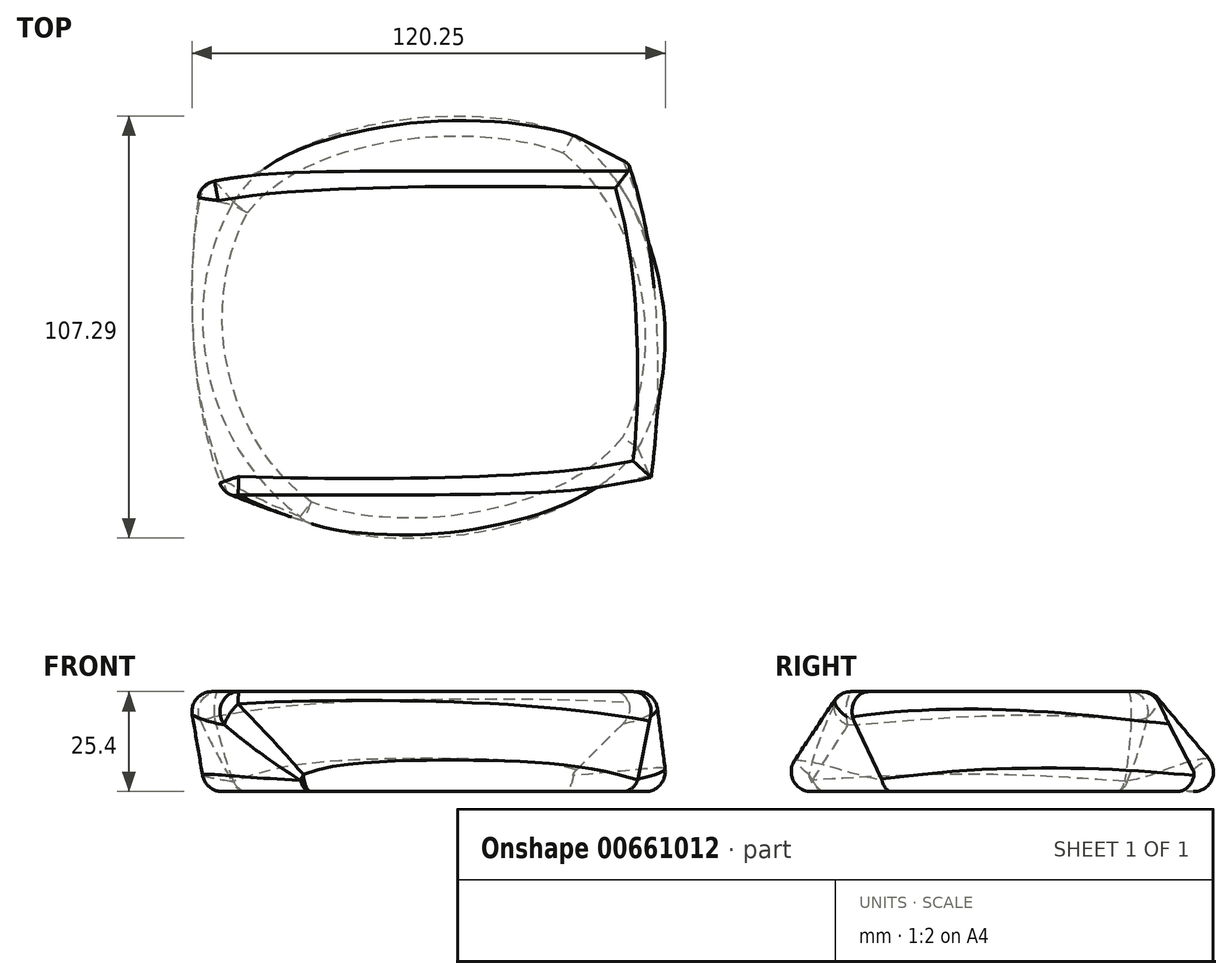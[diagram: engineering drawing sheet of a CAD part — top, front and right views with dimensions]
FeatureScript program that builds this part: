
annotation { "Feature Type Name" : "Feature", "Feature Type Description" : "" }
export const myFeature = defineFeature(function(context is Context, id is Id, definition is map)
    precondition{}
    {
        {
            var Q0;
            Q0=qCreatedBy(makeId("Top.planeOp"),FACE);
            var sketch = newSketch(context, id + "F0", { "sketchPlane" : qUnion([Q0])});
            skCircle(sketch, "E0", {"center": v(0, 0) * mm, "radius": 58.75 * mm});
            skSolve(sketch);
        }
        {
            var Q0;
            Q0=qCreatedBy(makeId("Top.planeOp"),FACE);
            cPlane(context, id + "F1", {"entities" : qUnion([Q0]), "cplaneType" : CPlaneType.OFFSET, "offset" : 25.4 * mm, "width" : 152.4 * mm, "height" : 152.4 * mm});
        }
        {
            var Q0;
            Q0=qCreatedBy(id+"F1.planeOp",FACE);
            var sketch = newSketch(context, id + "F2", { "sketchPlane" : qUnion([Q0])});
            skLineSegment(sketch, "E1.bottom", {"start": v(-63.13, 37.36) * mm, "end": v(55.54, 37.36) * mm});
            skLineSegment(sketch, "E1.top", {"start": v(-63.13, -41.93) * mm, "end": v(55.54, -41.93) * mm});
            skLineSegment(sketch, "E1.left", {"start": v(-63.13, 37.36) * mm, "end": v(-63.13, -41.93) * mm});
            skLineSegment(sketch, "E1.right", {"start": v(55.54, 37.36) * mm, "end": v(55.54, -41.93) * mm});
            skSolve(sketch);
        }
        {
            var Q0;
            Q0=makeQuery(id+"F2.imprint","IMPRINT",FACE,{"disambiguationData":[TD([[makeQuery(id+"F2.imprint","IMPRINT",EDGE,{"derivedFrom":sQuery(id+"F2.wireOp",EDGE,"E1.bottom")}),-1.0]])]});
            var Q1;
            Q1=makeQuery(id+"F0.imprint","IMPRINT",FACE,{"disambiguationData":[TD([[makeQuery(id+"F0.imprint","IMPRINT",EDGE,{"derivedFrom":sQuery(id+"F0.wireOp",EDGE,"E0")}),1.0]])]});
            loft(context, id + "F3", {"sheetProfilesArray" : [{ "sheetProfileEntities" : qUnion([Q0]) }, { "sheetProfileEntities" : qUnion([Q1]) }]});
        }
        {
            var Q0;
            Q0=makeQuery(id+"F3.opLoft","MID_CAP_EDGE",EDGE,{"disambiguationData":[OSD([sQuery(id+"F2.wireOp",EDGE,"E1.bottom"),sQuery(id+"F2.wireOp",EDGE,"E1.top"),sQuery(id+"F2.wireOp",EDGE,"E1.left")])],"capPos":0.0});
            var Q1;
            Q1=makeQuery(id+"F3.opLoft","MID_CAP_EDGE",EDGE,{"disambiguationData":[OSD([sQuery(id+"F2.wireOp",EDGE,"E1.bottom"),sQuery(id+"F2.wireOp",EDGE,"E1.left"),sQuery(id+"F2.wireOp",EDGE,"E1.right")])],"capPos":0.0});
            var Q2;
            Q2=makeQuery(id+"F3.opLoft","MID_CAP_EDGE",EDGE,{"disambiguationData":[OSD([sQuery(id+"F2.wireOp",EDGE,"E1.bottom"),sQuery(id+"F2.wireOp",EDGE,"E1.top"),sQuery(id+"F2.wireOp",EDGE,"E1.right")])],"capPos":0.0});
            var Q3;
            Q3=makeQuery(id+"F3.opLoft","MID_CAP_EDGE",EDGE,{"disambiguationData":[OSD([sQuery(id+"F2.wireOp",EDGE,"E1.top"),sQuery(id+"F2.wireOp",EDGE,"E1.left"),sQuery(id+"F2.wireOp",EDGE,"E1.right")])],"capPos":0.0});
            fillet(context, id + "F4", {"entities" : qUnion([Q0, Q1, Q2, Q3]), "radius" : 5.08 * mm, "tangentPropagation" : true, "allowEdgeOverflow" : false});
        }
        {
            var Q0;
            Q0=makeQuery(id+"F3.opLoft","MID_CAP_EDGE",EDGE,{"disambiguationData":[OSD([sQuery(id+"F0.wireOp",EDGE,"E0"),sQuery(id+"F2.wireOp",EDGE,"E1.bottom"),sQuery(id+"F2.wireOp",EDGE,"E1.top"),sQuery(id+"F2.wireOp",EDGE,"E1.left"),sQuery(id+"F2.wireOp",EDGE,"E1.right")])],"capPos":1.0});
            var Q1;
            Q1=makeQuery(id+"F3.opLoft","MID_CAP_EDGE",EDGE,{"disambiguationData":[OSD([sQuery(id+"F0.wireOp",EDGE,"E0"),sQuery(id+"F2.wireOp",EDGE,"E1.bottom"),sQuery(id+"F2.wireOp",EDGE,"E1.top"),sQuery(id+"F2.wireOp",EDGE,"E1.right")])],"capPos":1.0});
            var Q2;
            Q2=makeQuery(id+"F3.opLoft","MID_CAP_EDGE",EDGE,{"disambiguationData":[OSD([sQuery(id+"F0.wireOp",EDGE,"E0"),sQuery(id+"F2.wireOp",EDGE,"E1.bottom"),sQuery(id+"F2.wireOp",EDGE,"E1.left"),sQuery(id+"F2.wireOp",EDGE,"E1.right")])],"capPos":1.0});
            var Q3;
            Q3=makeQuery(id+"F3.opLoft","MID_CAP_EDGE",EDGE,{"disambiguationData":[OSD([sQuery(id+"F0.wireOp",EDGE,"E0"),sQuery(id+"F2.wireOp",EDGE,"E1.bottom"),sQuery(id+"F2.wireOp",EDGE,"E1.left")])],"capPos":1.0});
            var Q4;
            Q4=makeQuery(id+"F3.opLoft","SWEPT_EDGE",EDGE,{"disambiguationData":[OSD([sQuery(id+"F0.wireOp",EDGE,"E0"),sQuery(id+"F2.wireOp",EDGE,"E1.top"),sQuery(id+"F2.wireOp",EDGE,"E1.left"),sQuery(id+"F2.wireOp",EDGE,"E1.right")])]});
            var Q5;
            Q5=makeQuery(id+"F3.opLoft","SWEPT_EDGE",EDGE,{"disambiguationData":[OSD([sQuery(id+"F2.wireOp",EDGE,"E1.bottom"),sQuery(id+"F2.wireOp",EDGE,"E1.left")])]});
            var Q6;
            {var subQ0=sQuery(id+"F2.wireOp",EDGE,"E1.left");var subQ1=sQuery(id+"F2.wireOp",EDGE,"E1.right");var subQ2=sQuery(id+"F2.wireOp",EDGE,"E1.top");var subQ3=sQuery(id+"F2.wireOp",EDGE,"E1.bottom");var subQ4=sQuery(id+"F0.wireOp",EDGE,"E0");Q6=makeQuery(id+"F4.opFillet","BLEND_EDGE",EDGE,{"blendedFrom":[makeQuery(id+"F3.opLoft","MID_CAP_EDGE",EDGE,{"disambiguationData":[OSD([subQ3,subQ2,subQ0])],"capPos":0.0}),makeQuery(id+"F3.opLoft","SWEPT_FACE",FACE,{"disambiguationData":[OSD([subQ4,subQ3,subQ2,subQ0,subQ1]),TDD([makeQuery(id+"F0.imprint","IMPRINT",EDGE,{"derivedFrom":subQ4}),makeQuery(id+"F2.imprint","INTERSECT",VERTEX,{"derivedFrom":[subQ3,subQ0]}),makeQuery(id+"F2.imprint","INTERSECT",VERTEX,{"derivedFrom":[subQ2,subQ0]}),makeQuery(id+"F2.imprint","INTERSECT",VERTEX,{"derivedFrom":[subQ2,subQ1]}),makeQuery(id+"F2.imprint","IMPRINT",EDGE,{"derivedFrom":subQ0})])]})],"blendedInto":[makeQuery(id+"F3.opLoft","SWEPT_FACE",FACE,{"disambiguationData":[OSD([subQ4,subQ3,subQ2,subQ0,subQ1]),TDD([makeQuery(id+"F0.imprint","IMPRINT",EDGE,{"derivedFrom":subQ4}),makeQuery(id+"F2.imprint","INTERSECT",VERTEX,{"derivedFrom":[subQ3,subQ0]}),makeQuery(id+"F2.imprint","INTERSECT",VERTEX,{"derivedFrom":[subQ2,subQ0]}),makeQuery(id+"F2.imprint","INTERSECT",VERTEX,{"derivedFrom":[subQ2,subQ1]}),makeQuery(id+"F2.imprint","IMPRINT",EDGE,{"derivedFrom":subQ0})])]})]});}
            var Q7;
            {var subQ0=sQuery(id+"F2.wireOp",EDGE,"E1.right");var subQ1=sQuery(id+"F2.wireOp",EDGE,"E1.top");var subQ2=sQuery(id+"F2.wireOp",EDGE,"E1.bottom");var subQ3=sQuery(id+"F2.wireOp",EDGE,"E1.left");var subQ4=sQuery(id+"F0.wireOp",EDGE,"E0");Q7=makeQuery(id+"F4.opFillet","BLEND_EDGE",EDGE,{"blendedFrom":[makeQuery(id+"F3.opLoft","MID_CAP_EDGE",EDGE,{"disambiguationData":[OSD([subQ2,subQ1,subQ0])],"capPos":0.0}),makeQuery(id+"F3.opLoft","SWEPT_FACE",FACE,{"disambiguationData":[OSD([subQ4,subQ2,subQ1,subQ3,subQ0]),TDD([makeQuery(id+"F0.imprint","IMPRINT",EDGE,{"derivedFrom":subQ4}),makeQuery(id+"F2.imprint","INTERSECT",VERTEX,{"derivedFrom":[subQ2,subQ3]}),makeQuery(id+"F2.imprint","INTERSECT",VERTEX,{"derivedFrom":[subQ2,subQ0]}),makeQuery(id+"F2.imprint","INTERSECT",VERTEX,{"derivedFrom":[subQ1,subQ0]}),makeQuery(id+"F2.imprint","IMPRINT",EDGE,{"derivedFrom":subQ0})])]})],"blendedInto":[makeQuery(id+"F3.opLoft","SWEPT_FACE",FACE,{"disambiguationData":[OSD([subQ4,subQ2,subQ1,subQ3,subQ0]),TDD([makeQuery(id+"F0.imprint","IMPRINT",EDGE,{"derivedFrom":subQ4}),makeQuery(id+"F2.imprint","INTERSECT",VERTEX,{"derivedFrom":[subQ2,subQ3]}),makeQuery(id+"F2.imprint","INTERSECT",VERTEX,{"derivedFrom":[subQ2,subQ0]}),makeQuery(id+"F2.imprint","INTERSECT",VERTEX,{"derivedFrom":[subQ1,subQ0]}),makeQuery(id+"F2.imprint","IMPRINT",EDGE,{"derivedFrom":subQ0})])]})]});}
            var Q8;
            {var subQ0=sQuery(id+"F2.wireOp",EDGE,"E1.bottom");var subQ1=sQuery(id+"F2.wireOp",EDGE,"E1.top");var subQ2=sQuery(id+"F2.wireOp",EDGE,"E1.right");Q8=makeQuery(id+"F4.opFillet","BLEND_EDGE",EDGE,{"blendedFrom":[makeQuery(id+"F3.opLoft","MID_CAP_EDGE",EDGE,{"disambiguationData":[OSD([subQ0,subQ1,subQ2])],"capPos":0.0}),makeQuery(id+"F3.opLoft","CAP_FACE",FACE,{"disambiguationData":[OSD([makeQuery(id+"F2.imprint","IMPRINT",FACE,{"disambiguationData":[TD([[makeQuery(id+"F2.imprint","IMPRINT",EDGE,{"derivedFrom":subQ0}),-1.0]])]})])],"isStart":true})],"blendedInto":[makeQuery(id+"F3.opLoft","CAP_FACE",FACE,{"disambiguationData":[OSD([makeQuery(id+"F2.imprint","IMPRINT",FACE,{"disambiguationData":[TD([[makeQuery(id+"F2.imprint","IMPRINT",EDGE,{"derivedFrom":subQ0}),-1.0]])]})])],"isStart":true})]});}
            fillet(context, id + "F5", {"entities" : qUnion([Q0, Q1, Q2, Q3, Q4, Q5, Q6, Q7, Q8]), "radius" : 5.08 * mm, "tangentPropagation" : true, "allowEdgeOverflow" : false});
        }
    });
